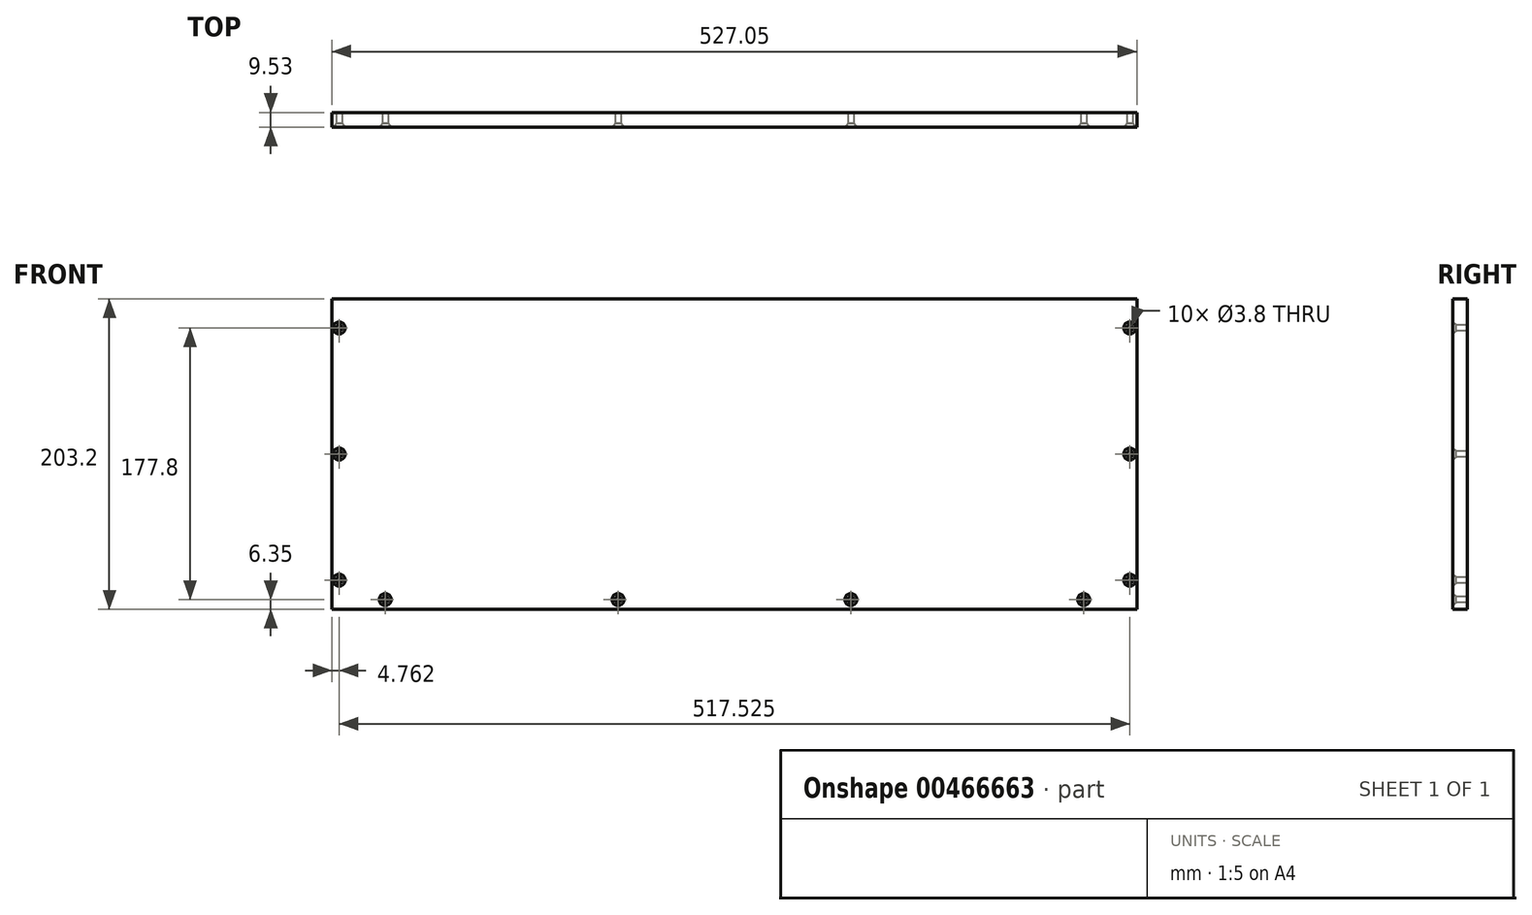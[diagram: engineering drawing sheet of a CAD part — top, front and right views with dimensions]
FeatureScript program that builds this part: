
annotation { "Feature Type Name" : "Feature", "Feature Type Description" : "" }
export const myFeature = defineFeature(function(context is Context, id is Id, definition is map)
    precondition{}
    {
        {
            var Q0;
            Q0=qCreatedBy(makeId("Front.planeOp"),FACE);
            var sketch = newSketch(context, id + "F0", { "sketchPlane" : qUnion([Q0])});
            skLineSegment(sketch, "E0.bottom", {"start": v(0, 0) * mm, "end": v(-527.05, 0) * mm});
            skLineSegment(sketch, "E0.top", {"start": v(0, 203.2) * mm, "end": v(-527.05, 203.2) * mm});
            skLineSegment(sketch, "E0.left", {"start": v(0, 0) * mm, "end": v(0, 203.2) * mm});
            skLineSegment(sketch, "E0.right", {"start": v(-527.05, 0) * mm, "end": v(-527.05, 203.2) * mm});
            skSolve(sketch);
        }
        {
            var Q0;
            Q0 = qSketchRegion(id + "F0", true);
            extrude(context, id + "F1", {"entities" : qUnion([Q0]), "depth" : 9.52 * mm});
        }
        {
            var Q0;
            Q0=makeQuery(id+"F1.opExtrude","CAP_FACE",FACE,{"disambiguationData":[OSD([sQuery(id+"F0.wireOp",EDGE,"E0.bottom"),sQuery(id+"F0.wireOp",EDGE,"E0.top"),sQuery(id+"F0.wireOp",EDGE,"E0.left"),sQuery(id+"F0.wireOp",EDGE,"E0.right")])],"isStart":false});
            var sketch = newSketch(context, id + "F2", { "sketchPlane" : qUnion([Q0])});
            skPoint(sketch, "E1", {"position": v(-492.13, 6.35) * mm});
            skPoint(sketch, "E2", {"position": v(-522.29, 19.05) * mm});
            skPoint(sketch, "E3", {"position": v(-4.76, 19.05) * mm});
            skPoint(sketch, "E4.1.0.0", {"position": v(-339.73, 6.35) * mm});
            skPoint(sketch, "E4.2.0.0", {"position": v(-187.33, 6.35) * mm});
            skPoint(sketch, "E4.3.0.0", {"position": v(-34.92, 6.35) * mm});
            skLineSegment(sketch, "E4.direction1", {"start": v(-492.13, 6.35) * mm, "end": v(-339.73, 6.35) * mm, "construction": true});
            skPoint(sketch, "E5.0.1.0", {"position": v(-522.29, 101.6) * mm});
            skPoint(sketch, "E5.0.2.0", {"position": v(-522.29, 184.15) * mm});
            skLineSegment(sketch, "E5.direction1", {"start": v(-519.11, 19.05) * mm, "end": v(-493.71, 19.05) * mm, "construction": true});
            skLineSegment(sketch, "E5.direction2", {"start": v(-519.11, 19.05) * mm, "end": v(-519.11, 101.6) * mm, "construction": true});
            skPoint(sketch, "E6.0.1.0", {"position": v(-4.76, 101.6) * mm});
            skPoint(sketch, "E6.0.2.0", {"position": v(-4.76, 184.15) * mm});
            skLineSegment(sketch, "E6.direction1", {"start": v(-4.76, 19.05) * mm, "end": v(20.64, 19.05) * mm, "construction": true});
            skLineSegment(sketch, "E6.direction2", {"start": v(-4.76, 19.05) * mm, "end": v(-4.76, 101.6) * mm, "construction": true});
            skSolve(sketch);
        }
        {
            var Q0;
            Q0=sQuery(id+"F2.wireOp",VERTEX,"E5.0.2.0");
            var Q1;
            Q1=sQuery(id+"F2.wireOp",VERTEX,"E5.0.1.0");
            var Q2;
            Q2=sQuery(id+"F2.wireOp",VERTEX,"E2");
            var Q3;
            Q3=sQuery(id+"F2.wireOp",VERTEX,"E1");
            var Q4;
            Q4=sQuery(id+"F2.wireOp",VERTEX,"E4.1.0.0");
            var Q5;
            Q5=sQuery(id+"F2.wireOp",VERTEX,"E4.2.0.0");
            var Q6;
            Q6=sQuery(id+"F2.wireOp",VERTEX,"E4.3.0.0");
            var Q7;
            Q7=sQuery(id+"F2.wireOp",VERTEX,"E3");
            var Q8;
            Q8=sQuery(id+"F2.wireOp",VERTEX,"E6.0.1.0");
            var Q9;
            Q9=sQuery(id+"F2.wireOp",VERTEX,"E6.0.2.0");
            var Q10;
            Q10=makeQuery(id+"F1.opExtrude","SWEPT_BODY",BODY,{"disambiguationData":[OSD([sQuery(id+"F0.wireOp",EDGE,"E0.bottom"),sQuery(id+"F0.wireOp",EDGE,"E0.top"),sQuery(id+"F0.wireOp",EDGE,"E0.left"),sQuery(id+"F0.wireOp",EDGE,"E0.right")])]});
            hole(context, id + "F3", {"style" : HoleStyle.C_SINK, "endStyle" : HoleEndStyle.BLIND, "standardTappedOrClearance" : lookupTablePath({ "standard" : "ANSI", "fit" : "Normal (ASME)", "size" : "#6", "type" : "Clearance" }), "standardBlindInLast" : lookupTablePath({ "fit" : "Free", "standard" : "ANSI", "size" : "#6", "type" : "Clearance" }), "holeDiameter" : 3.8 * mm, "cSinkDiameter" : 7.8 * mm, "cSinkAngle" : 82 * degree, "holeDepth" : 13.5 * mm, "isTappedThrough" : true, "tappedDepth" : 9.52 * mm, "tapClearance" : 5, "locations" : qUnion([Q0, Q1, Q2, Q3, Q4, Q5, Q6, Q7, Q8, Q9]), "scope" : qUnion([Q10])});
        }
    });
